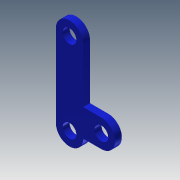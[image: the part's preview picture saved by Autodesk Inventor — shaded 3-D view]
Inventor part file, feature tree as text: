
AUTODESK INVENTOR PART (.ipt)
format: ipt  version: 2013 (Build 170138000, 138)  size: 168,960 bytes
history: native  units: mm
features: extrude x8, sketch x8
ambient origin geometry x8: Origin, YZ Plane, XZ Plane, XY Plane, X Axis, Y Axis, Z Axis, Center Point
bodies: Solid1 (feature_tree)
feature tree (16):
  extrude  "Extrusion1"  Depth=18.0mm
  extrude  "Extrusion2"  Depth=6.0mm
  extrude  "Extrusion3"  Depth=4.0mm
  extrude  "Extrusion4"  Depth=3.0mm
  extrude  "Extrusion5"  Depth=1.5mm TaperAngle=0.0deg
  extrude  "Extrusion6"  Depth=3.0mm
  extrude  "Extrusion7"  Depth=6.0mm
  extrude  "Extrusion8"  Depth=4.0mm
  sketch  "Sketch1"  dims[d0=6.0mm d1=18.0mm]
  sketch  "Sketch2"  dims[d2=6.0mm d4=6.0mm]
  sketch  "Sketch3"  dims[d5=4.0mm d6=4.0mm]
  sketch  "Sketch4"  dims[d7=2.0mm d10=3.0mm]
  sketch  "Sketch5"  dims[d11=6.0mm d12=1.5mm d13=0.0mm]
  sketch  "Sketch6"  dims[d14=3.0mm d15=3.0mm]
  sketch  "Sketch7"  dims[d16=4.0mm d17=6.0mm]
  sketch  "Sketch8"  dims[d18=1.5mm d19=0.0mm d20=4.0mm d21=6.0mm d22=4.0mm d23=1.5mm d24=0.0mm d25=3.0mm d26=1.5mm d27=0.0mm d28=0.2mm d29=0.2mm d30=0.2mm d31=1.5mm d32=0.0mm d33=3.0mm d34=3.0mm d35=3.0mm d36=2.0mm d37=0.0mm d38=4.0mm d39=3.0mm d40=2.0mm d41=0.0mm d42=2.0mm d43=0.0mm]
